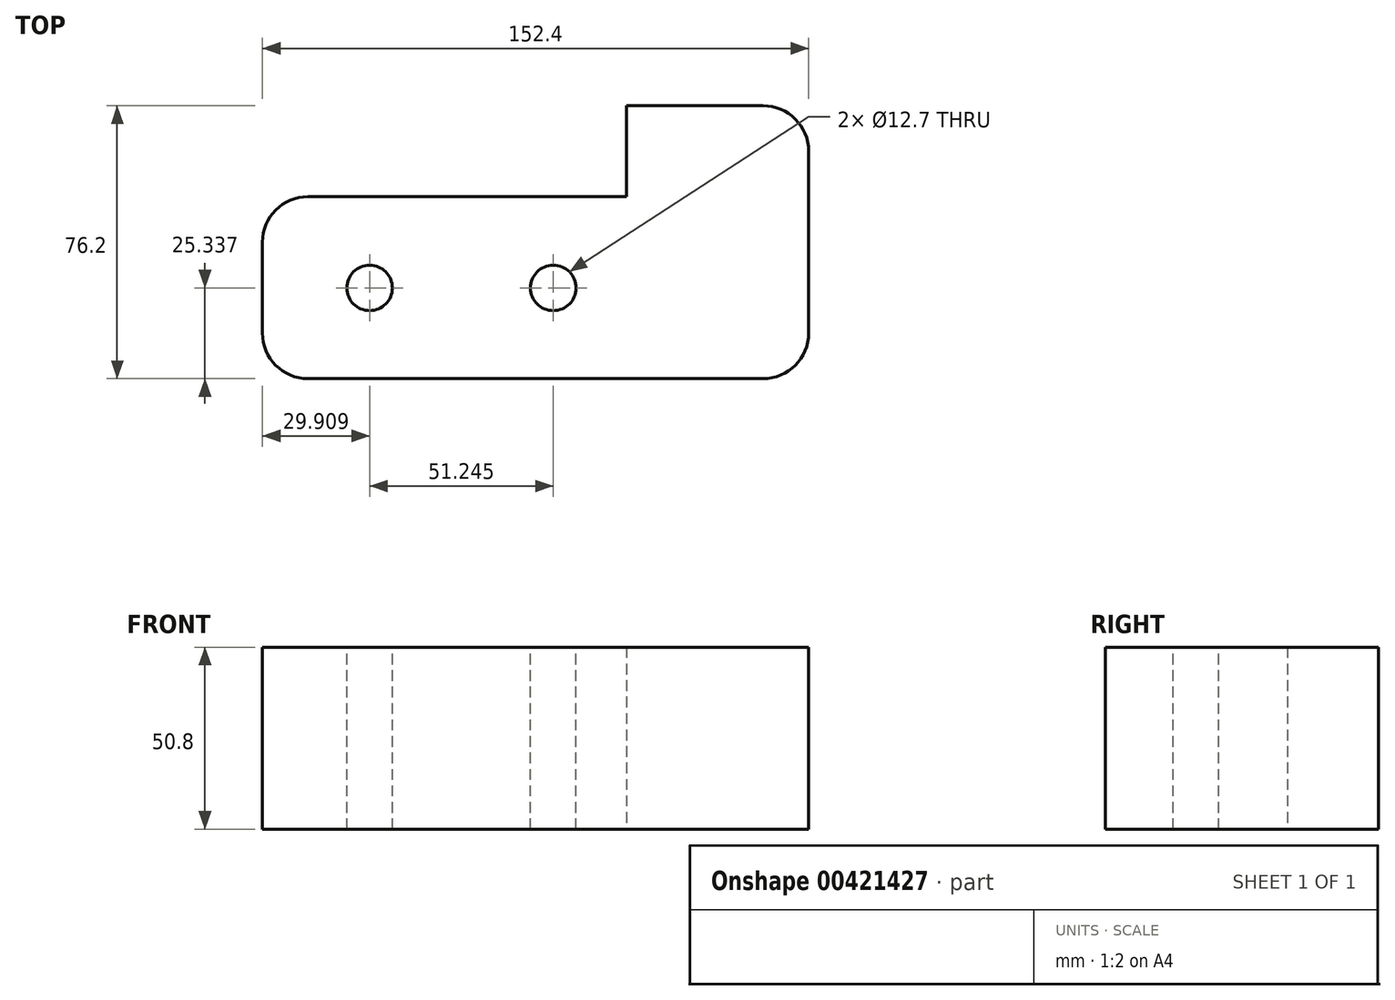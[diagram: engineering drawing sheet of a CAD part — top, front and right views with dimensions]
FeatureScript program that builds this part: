
annotation { "Feature Type Name" : "Feature", "Feature Type Description" : "" }
export const myFeature = defineFeature(function(context is Context, id is Id, definition is map)
    precondition{}
    {
        {
            var Q0;
            Q0=qCreatedBy(makeId("Top.planeOp"),FACE);
            var sketch = newSketch(context, id + "F0", { "sketchPlane" : qUnion([Q0])});
            skLineSegment(sketch, "E0", {"start": v(0, 0) * mm, "end": v(152.4, 0) * mm});
            skLineSegment(sketch, "E1", {"start": v(0, 0) * mm, "end": v(0, 50.8) * mm});
            skLineSegment(sketch, "E2", {"start": v(0, 50.8) * mm, "end": v(101.6, 50.8) * mm});
            skLineSegment(sketch, "E3", {"start": v(101.6, 50.8) * mm, "end": v(101.6, 76.2) * mm});
            skLineSegment(sketch, "E4", {"start": v(101.6, 76.2) * mm, "end": v(152.4, 76.2) * mm});
            skLineSegment(sketch, "E5", {"start": v(152.4, 76.2) * mm, "end": v(152.4, 0) * mm});
            skSolve(sketch);
        }
        {
            var Q0;
            Q0=makeQuery(id+"F0.imprint","IMPRINT",FACE,{"disambiguationData":[TD([[makeQuery(id+"F0.imprint","IMPRINT",EDGE,{"derivedFrom":sQuery(id+"F0.wireOp",EDGE,"E0")}),1.0]])]});
            extrude(context, id + "F1", {"entities" : qUnion([Q0]), "depth" : 50.8 * mm});
        }
        {
            var Q0;
            Q0=makeQuery(id+"F1.opExtrude","SWEPT_EDGE",EDGE,{"disambiguationData":[OSD([sQuery(id+"F0.wireOp",EDGE,"E4"),sQuery(id+"F0.wireOp",EDGE,"E5")])]});
            fillet(context, id + "F2", {"entities" : qUnion([Q0]), "radius" : 12.7 * mm, "tangentPropagation" : true, "allowEdgeOverflow" : false});
        }
        {
            var Q0;
            Q0=makeQuery(id+"F1.opExtrude","SWEPT_EDGE",EDGE,{"disambiguationData":[OSD([sQuery(id+"F0.wireOp",EDGE,"E1"),sQuery(id+"F0.wireOp",EDGE,"E2")])]});
            fillet(context, id + "F3", {"entities" : qUnion([Q0]), "radius" : 12.7 * mm, "tangentPropagation" : true, "allowEdgeOverflow" : false});
        }
        {
            var Q0;
            Q0=makeQuery(id+"F1.opExtrude","SWEPT_EDGE",EDGE,{"disambiguationData":[OSD([sQuery(id+"F0.wireOp",EDGE,"E0"),sQuery(id+"F0.wireOp",EDGE,"E1")])]});
            var Q1;
            Q1=makeQuery(id+"F1.opExtrude","SWEPT_EDGE",EDGE,{"disambiguationData":[OSD([sQuery(id+"F0.wireOp",EDGE,"E0"),sQuery(id+"F0.wireOp",EDGE,"E5")])]});
            fillet(context, id + "F4", {"entities" : qUnion([Q0, Q1]), "radius" : 12.7 * mm, "tangentPropagation" : true, "allowEdgeOverflow" : false});
        }
        {
            var Q0;
            Q0=makeQuery(id+"F1.opExtrude","CAP_FACE",FACE,{"disambiguationData":[OSD([sQuery(id+"F0.wireOp",EDGE,"E0"),sQuery(id+"F0.wireOp",EDGE,"E1"),sQuery(id+"F0.wireOp",EDGE,"E2"),sQuery(id+"F0.wireOp",EDGE,"E3"),sQuery(id+"F0.wireOp",EDGE,"E4"),sQuery(id+"F0.wireOp",EDGE,"E5")])],"isStart":false});
            var sketch = newSketch(context, id + "F5", { "sketchPlane" : qUnion([Q0])});
            skPoint(sketch, "E6", {"position": v(30.1, 25.4) * mm});
            skPoint(sketch, "E6.positionSnap0", {"position": v(0, 25.4) * mm});
            skPoint(sketch, "E7", {"position": v(80.9, 25.4) * mm});
            skSolve(sketch);
        }
        {
            var Q0;
            {var subQ2=sQuery(id+"F0.wireOp",EDGE,"E3");Q0=makeQuery(id+"F5.imprint","IMPRINT",FACE,{"disambiguationData":[TD([[makeQuery(id+"F5.imprint","IMPRINT",EDGE,{"derivedFrom":makeQuery(id+"F1.opExtrude","CAP_EDGE",EDGE,{"disambiguationData":[OSD([subQ2])],"isStart":false})}),-1.0]])]});}
            var sketch = newSketch(context, id + "F6", { "sketchPlane" : qUnion([Q0])});
            skPoint(sketch, "E8", {"position": v(29.9, 25.34) * mm});
            skPoint(sketch, "E9", {"position": v(81.15, 25.34) * mm});
            skSolve(sketch);
        }
        {
            var Q0;
            Q0=sQuery(id+"F6.wireOp",VERTEX,"E8");
            var Q1;
            Q1=sQuery(id+"F6.wireOp",VERTEX,"E9");
            var Q2;
            Q2=makeQuery(id+"F1.opExtrude","SWEPT_BODY",BODY,{"disambiguationData":[OSD([sQuery(id+"F0.wireOp",EDGE,"E0"),sQuery(id+"F0.wireOp",EDGE,"E1"),sQuery(id+"F0.wireOp",EDGE,"E2"),sQuery(id+"F0.wireOp",EDGE,"E3"),sQuery(id+"F0.wireOp",EDGE,"E4"),sQuery(id+"F0.wireOp",EDGE,"E5")])]});
            hole(context, id + "F7", {"style" : HoleStyle.SIMPLE, "endStyle" : HoleEndStyle.THROUGH, "holeDiameter" : 12.7 * mm, "isTappedThrough" : true, "tappedDepth" : 12.7 * mm, "tapClearance" : 3, "locations" : qUnion([Q0, Q1]), "scope" : qUnion([Q2])});
        }
    });
